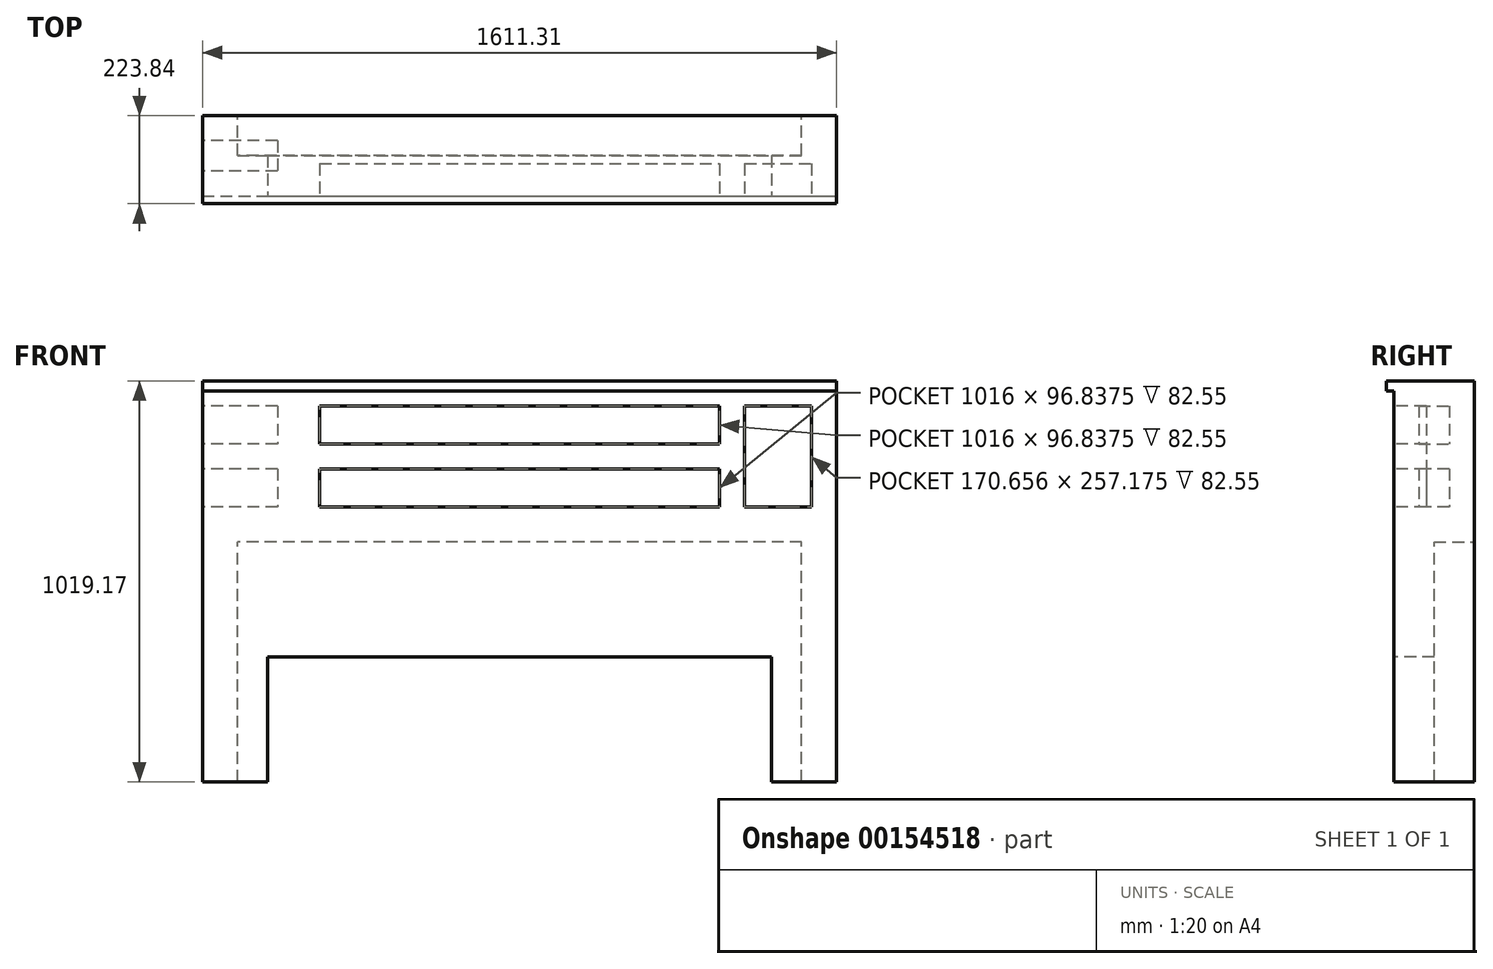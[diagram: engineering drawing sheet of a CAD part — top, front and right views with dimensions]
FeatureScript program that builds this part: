
annotation { "Feature Type Name" : "Feature", "Feature Type Description" : "" }
export const myFeature = defineFeature(function(context is Context, id is Id, definition is map)
    precondition{}
    {
        {
            var Q0;
            Q0=qCreatedBy(makeId("Front.planeOp"),FACE);
            var sketch = newSketch(context, id + "F0", { "sketchPlane" : qUnion([Q0])});
            skLineSegment(sketch, "E0.bottom", {"start": v(0, 0) * mm, "end": v(1611.31, 0) * mm});
            skLineSegment(sketch, "E0.top", {"start": v(0, 1019.18) * mm, "end": v(1611.31, 1019.18) * mm});
            skLineSegment(sketch, "E0.left", {"start": v(0, 0) * mm, "end": v(0, 1019.18) * mm});
            skLineSegment(sketch, "E0.right", {"start": v(1611.31, 0) * mm, "end": v(1611.31, 1019.18) * mm});
            skLineSegment(sketch, "E1.bottom", {"start": v(165.9, 0) * mm, "end": v(1445.42, 0) * mm});
            skLineSegment(sketch, "E1.top", {"start": v(165.9, 317.5) * mm, "end": v(1445.42, 317.5) * mm});
            skLineSegment(sketch, "E1.left", {"start": v(165.9, 0) * mm, "end": v(165.9, 317.5) * mm});
            skLineSegment(sketch, "E1.right", {"start": v(1445.42, 0) * mm, "end": v(1445.42, 317.5) * mm});
            skLineSegment(sketch, "E2", {"start": v(165.9, 158.75) * mm, "end": v(0, 158.75) * mm, "construction": true});
            skLineSegment(sketch, "E3", {"start": v(1445.42, 158.75) * mm, "end": v(1611.31, 158.75) * mm, "construction": true});
            skLineSegment(sketch, "E4", {"start": v(0, 993.78) * mm, "end": v(1611.31, 993.78) * mm});
            skLineSegment(sketch, "E5", {"start": v(0, 698.5) * mm, "end": v(1611.31, 698.5) * mm});
            skLineSegment(sketch, "E6.bottom", {"start": v(297.66, 955.68) * mm, "end": v(1313.66, 955.68) * mm});
            skLineSegment(sketch, "E6.top", {"start": v(297.66, 858.84) * mm, "end": v(1313.66, 858.84) * mm});
            skLineSegment(sketch, "E6.left", {"start": v(297.66, 955.68) * mm, "end": v(297.66, 858.84) * mm});
            skLineSegment(sketch, "E6.right", {"start": v(1313.66, 955.68) * mm, "end": v(1313.66, 858.84) * mm});
            skLineSegment(sketch, "E7.bottom", {"start": v(1313.66, 795.34) * mm, "end": v(297.66, 795.34) * mm});
            skLineSegment(sketch, "E7.top", {"start": v(1313.66, 698.5) * mm, "end": v(297.66, 698.5) * mm});
            skLineSegment(sketch, "E7.left", {"start": v(1313.66, 795.34) * mm, "end": v(1313.66, 698.5) * mm});
            skLineSegment(sketch, "E7.right", {"start": v(297.66, 795.34) * mm, "end": v(297.66, 698.5) * mm});
            skLineSegment(sketch, "E8", {"start": v(297.66, 907.26) * mm, "end": v(0, 907.26) * mm, "construction": true});
            skLineSegment(sketch, "E9", {"start": v(1313.66, 907.26) * mm, "end": v(1611.31, 907.26) * mm, "construction": true});
            skLineSegment(sketch, "E10.bottom", {"start": v(1377.16, 955.68) * mm, "end": v(1547.81, 955.68) * mm});
            skLineSegment(sketch, "E10.top", {"start": v(1377.16, 698.5) * mm, "end": v(1547.81, 698.5) * mm});
            skLineSegment(sketch, "E10.left", {"start": v(1377.16, 955.68) * mm, "end": v(1377.16, 698.5) * mm});
            skLineSegment(sketch, "E10.right", {"start": v(1547.81, 955.68) * mm, "end": v(1547.81, 698.5) * mm});
            skSolve(sketch);
        }
        {
            var Q0;
            Q0=makeQuery(id+"F0.imprint","IMPRINT",FACE,{"disambiguationData":[TD([[makeQuery(id+"F0.imprint","IMPRINT",EDGE,{"derivedFrom":sQuery(id+"F0.wireOp",EDGE,"E0.bottom")}),1.0]])]});
            var Q1;
            {var subQ0=sQuery(id+"F0.wireOp",EDGE,"E4");Q1=makeQuery(id+"F0.imprint","IMPRINT",FACE,{"disambiguationData":[TD([[makeQuery(id+"F0.imprint","IMPRINT",EDGE,{"derivedFrom":subQ0}),-1.0]])]});}
            var Q2;
            Q2=makeQuery(id+"F0.imprint","IMPRINT",FACE,{"disambiguationData":[TD([[makeQuery(id+"F0.imprint","IMPRINT",EDGE,{"derivedFrom":sQuery(id+"F0.wireOp",EDGE,"E7.bottom")}),1.0]])]});
            var Q3;
            Q3=makeQuery(id+"F0.imprint","IMPRINT",FACE,{"disambiguationData":[TD([[makeQuery(id+"F0.imprint","IMPRINT",EDGE,{"derivedFrom":sQuery(id+"F0.wireOp",EDGE,"E6.bottom")}),-1.0]])]});
            var Q4;
            {var subQ0=sQuery(id+"F0.wireOp",EDGE,"E0.top");Q4=makeQuery(id+"F0.imprint","IMPRINT",FACE,{"disambiguationData":[TD([[makeQuery(id+"F0.imprint","IMPRINT",EDGE,{"derivedFrom":subQ0}),-1.0]])]});}
            var Q5;
            Q5=makeQuery(id+"F0.imprint","IMPRINT",FACE,{"disambiguationData":[TD([[makeQuery(id+"F0.imprint","IMPRINT",EDGE,{"derivedFrom":sQuery(id+"F0.wireOp",EDGE,"E10.bottom")}),-1.0]])]});
            extrude(context, id + "F1", {"entities" : qUnion([Q0, Q1, Q2, Q3, Q4, Q5]), "oppositeDirection" : true, "depth" : 223.84 * mm});
        }
        {
            var Q0;
            Q0=makeQuery(id+"F0.imprint","IMPRINT",FACE,{"disambiguationData":[TD([[makeQuery(id+"F0.imprint","IMPRINT",EDGE,{"derivedFrom":sQuery(id+"F0.wireOp",EDGE,"E6.bottom")}),-1.0]])]});
            var Q1;
            Q1=makeQuery(id+"F0.imprint","IMPRINT",FACE,{"disambiguationData":[TD([[makeQuery(id+"F0.imprint","IMPRINT",EDGE,{"derivedFrom":sQuery(id+"F0.wireOp",EDGE,"E7.bottom")}),1.0]])]});
            var Q2;
            Q2=makeQuery(id+"F0.imprint","IMPRINT",FACE,{"disambiguationData":[TD([[makeQuery(id+"F0.imprint","IMPRINT",EDGE,{"derivedFrom":sQuery(id+"F0.wireOp",EDGE,"E10.bottom")}),-1.0]])]});
            extrude(context, id + "F2", {"entities" : qUnion([Q0, Q1, Q2]), "operationType" : NewBodyOperationType.REMOVE, "oppositeDirection" : true, "depth" : 101.6 * mm});
        }
        {
            var Q0;
            Q0=makeQuery(id+"F0.imprint","IMPRINT",FACE,{"disambiguationData":[TD([[makeQuery(id+"F0.imprint","IMPRINT",EDGE,{"derivedFrom":sQuery(id+"F0.wireOp",EDGE,"E1.top")}),1.0]])]});
            var Q1;
            {var subQ0=sQuery(id+"F0.wireOp",EDGE,"E4");Q1=makeQuery(id+"F0.imprint","IMPRINT",FACE,{"disambiguationData":[TD([[makeQuery(id+"F0.imprint","IMPRINT",EDGE,{"derivedFrom":subQ0}),-1.0]])]});}
            extrude(context, id + "F3", {"entities" : qUnion([Q0, Q1]), "operationType" : NewBodyOperationType.REMOVE, "oppositeDirection" : true, "depth" : 19.05 * mm});
        }
        {
            var Q0;
            Q0=makeQuery(id+"F1.opExtrude","SWEPT_FACE",FACE,{"disambiguationData":[OSD([sQuery(id+"F0.wireOp",EDGE,"E0.left")])]});
            var sketch = newSketch(context, id + "F4", { "sketchPlane" : qUnion([Q0])});
            skLineSegment(sketch, "E11.bottom", {"start": v(-82.55, 955.68) * mm, "end": v(-160.34, 955.68) * mm});
            skLineSegment(sketch, "E11.top", {"start": v(-82.55, 858.84) * mm, "end": v(-160.34, 858.84) * mm});
            skLineSegment(sketch, "E11.left", {"start": v(-82.55, 955.68) * mm, "end": v(-82.55, 858.84) * mm});
            skLineSegment(sketch, "E11.right", {"start": v(-160.34, 955.68) * mm, "end": v(-160.34, 858.84) * mm});
            skLineSegment(sketch, "E12.bottom", {"start": v(-160.34, 795.34) * mm, "end": v(-82.55, 795.34) * mm});
            skLineSegment(sketch, "E12.top", {"start": v(-160.34, 698.5) * mm, "end": v(-82.55, 698.5) * mm});
            skLineSegment(sketch, "E12.left", {"start": v(-160.34, 795.34) * mm, "end": v(-160.34, 698.5) * mm});
            skLineSegment(sketch, "E12.right", {"start": v(-82.55, 795.34) * mm, "end": v(-82.55, 698.5) * mm});
            skSolve(sketch);
        }
        {
            var Q0;
            Q0=makeQuery(id+"F4.imprint","IMPRINT",FACE,{"disambiguationData":[TD([[makeQuery(id+"F4.imprint","IMPRINT",EDGE,{"derivedFrom":sQuery(id+"F4.wireOp",EDGE,"E11.bottom")}),1.0]])]});
            var Q1;
            Q1=makeQuery(id+"F4.imprint","IMPRINT",FACE,{"disambiguationData":[TD([[makeQuery(id+"F4.imprint","IMPRINT",EDGE,{"derivedFrom":sQuery(id+"F4.wireOp",EDGE,"E12.bottom")}),-1.0]])]});
            extrude(context, id + "F5", {"entities" : qUnion([Q0, Q1]), "operationType" : NewBodyOperationType.REMOVE, "oppositeDirection" : true, "depth" : 190.5 * mm});
        }
        {
            var Q0;
            Q0=makeQuery(id+"F1.opExtrude","CAP_FACE",FACE,{"disambiguationData":[OSD([sQuery(id+"F0.wireOp",EDGE,"E0.bottom"),sQuery(id+"F0.wireOp",EDGE,"E0.top"),sQuery(id+"F0.wireOp",EDGE,"E0.left"),sQuery(id+"F0.wireOp",EDGE,"E0.right"),sQuery(id+"F0.wireOp",EDGE,"E1.top"),sQuery(id+"F0.wireOp",EDGE,"E1.left"),sQuery(id+"F0.wireOp",EDGE,"E1.right")])],"isStart":false});
            var sketch = newSketch(context, id + "F6", { "sketchPlane" : qUnion([Q0])});
            skLineSegment(sketch, "E13.bottom", {"start": v(-1522.41, 0) * mm, "end": v(-88.9, 0) * mm});
            skLineSegment(sketch, "E13.top", {"start": v(-1522.41, 609.6) * mm, "end": v(-88.9, 609.6) * mm});
            skLineSegment(sketch, "E13.left", {"start": v(-1522.41, 0) * mm, "end": v(-1522.41, 609.6) * mm});
            skLineSegment(sketch, "E13.right", {"start": v(-88.9, 0) * mm, "end": v(-88.9, 609.6) * mm});
            skSolve(sketch);
        }
        {
            var Q0;
            Q0=makeQuery(id+"F6.imprint","IMPRINT",FACE,{"disambiguationData":[TD([[makeQuery(id+"F6.imprint","IMPRINT",EDGE,{"derivedFrom":sQuery(id+"F6.wireOp",EDGE,"E13.top")}),-1.0]])]});
            extrude(context, id + "F7", {"entities" : qUnion([Q0]), "operationType" : NewBodyOperationType.REMOVE, "oppositeDirection" : true, "depth" : 101.6 * mm});
        }
    });
